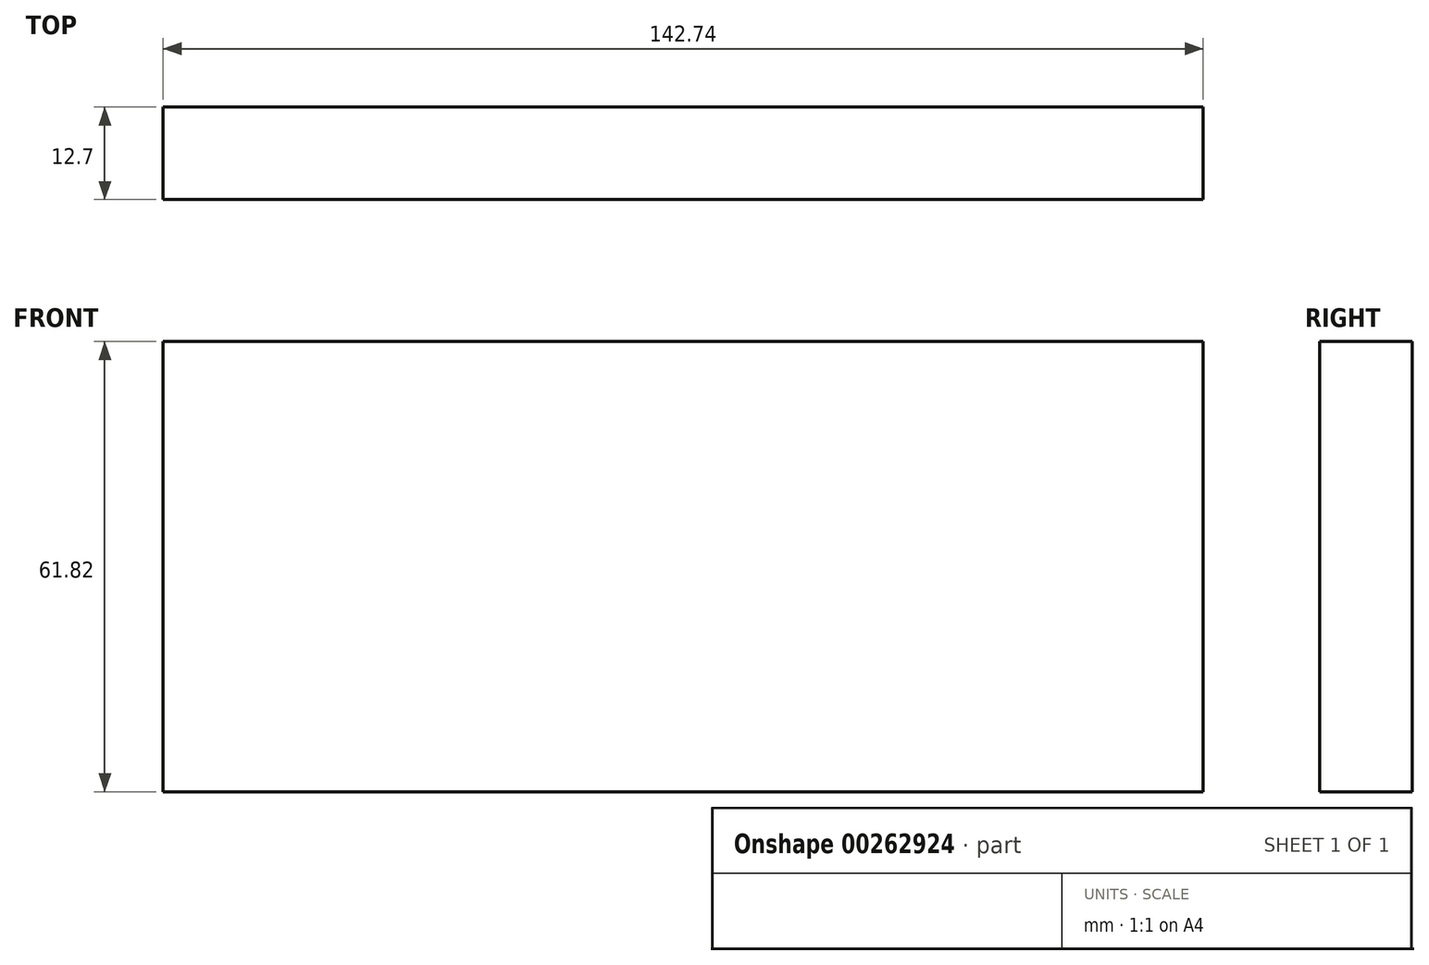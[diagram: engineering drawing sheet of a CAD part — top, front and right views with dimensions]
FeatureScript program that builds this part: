
annotation { "Feature Type Name" : "Feature", "Feature Type Description" : "" }
export const myFeature = defineFeature(function(context is Context, id is Id, definition is map)
    precondition{}
    {
        {
            var Q0;
            Q0=qCreatedBy(makeId("Front.planeOp"),FACE);
            var sketch = newSketch(context, id + "F0", { "sketchPlane" : qUnion([Q0])});
            skLineSegment(sketch, "E0.bottom", {"start": v(71.37, -30.91) * mm, "end": v(-71.37, -30.91) * mm});
            skLineSegment(sketch, "E0.top", {"start": v(71.37, 30.91) * mm, "end": v(-71.37, 30.91) * mm});
            skLineSegment(sketch, "E0.left", {"start": v(71.37, -30.91) * mm, "end": v(71.37, 30.91) * mm});
            skLineSegment(sketch, "E0.right", {"start": v(-71.37, -30.91) * mm, "end": v(-71.37, 30.91) * mm});
            skPoint(sketch, "E0.middle", {"position": v(0, 0) * mm});
            skSolve(sketch);
        }
        {
            var Q0;
            Q0 = qSketchRegion(id + "F0", true);
            extrude(context, id + "F1", {"entities" : qUnion([Q0]), "depth" : 12.7 * mm});
        }
    });
